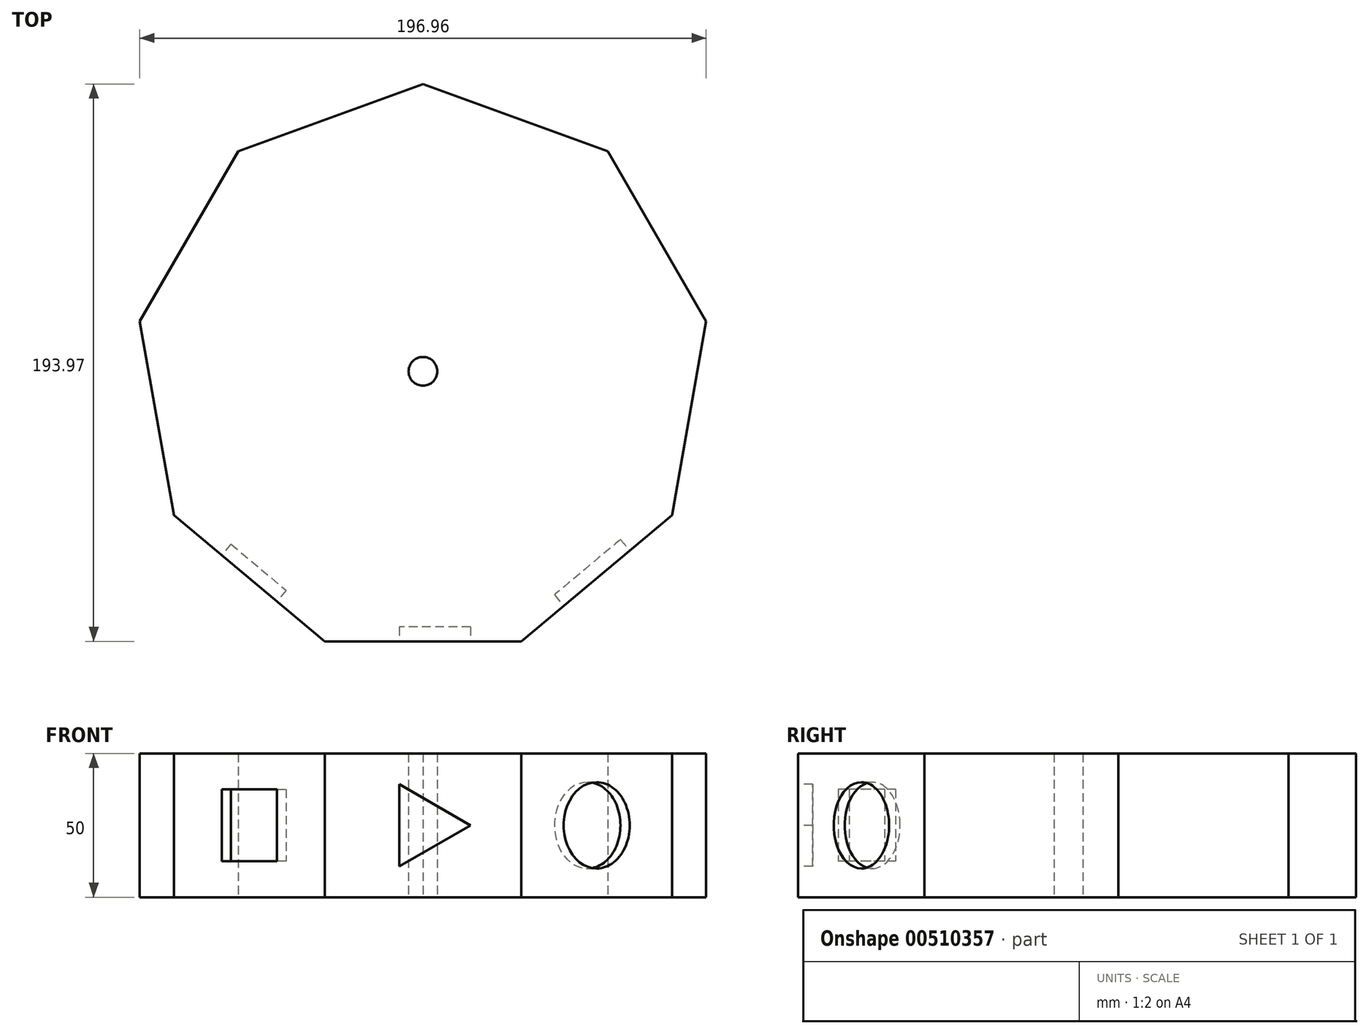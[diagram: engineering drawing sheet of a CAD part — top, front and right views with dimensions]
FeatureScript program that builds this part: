
annotation { "Feature Type Name" : "Feature", "Feature Type Description" : "" }
export const myFeature = defineFeature(function(context is Context, id is Id, definition is map)
    precondition{}
    {
        {
            var Q0;
            Q0=qCreatedBy(makeId("Top.planeOp"),FACE);
            var sketch = newSketch(context, id + "F0", { "sketchPlane" : qUnion([Q0])});
            skCircle(sketch, "E0.cCircle", {"center": v(0, 0) * mm, "radius": 100 * mm, "construction": true});
            skLineSegment(sketch, "E0.0", {"start": v(0, 100) * mm, "end": v(64.28, 76.6) * mm});
            skLineSegment(sketch, "E0.1", {"start": v(64.28, 76.6) * mm, "end": v(98.48, 17.36) * mm});
            skLineSegment(sketch, "E0.2", {"start": v(98.48, 17.36) * mm, "end": v(86.6, -50) * mm});
            skLineSegment(sketch, "E0.3", {"start": v(86.6, -50) * mm, "end": v(34.2, -93.97) * mm});
            skLineSegment(sketch, "E0.4", {"start": v(34.2, -93.97) * mm, "end": v(-34.2, -93.97) * mm});
            skLineSegment(sketch, "E0.5", {"start": v(-34.2, -93.97) * mm, "end": v(-86.6, -50) * mm});
            skLineSegment(sketch, "E0.6", {"start": v(-86.6, -50) * mm, "end": v(-98.48, 17.36) * mm});
            skLineSegment(sketch, "E0.7", {"start": v(-98.48, 17.36) * mm, "end": v(-64.28, 76.6) * mm});
            skLineSegment(sketch, "E0.8", {"start": v(-64.28, 76.6) * mm, "end": v(0, 100) * mm});
            skCircle(sketch, "E1", {"center": v(0, 0) * mm, "radius": 5 * mm});
            skSolve(sketch);
        }
        {
            var Q0;
            Q0=makeQuery(id+"F0.imprint","IMPRINT",FACE,{"disambiguationData":[TD([[makeQuery(id+"F0.imprint","IMPRINT",EDGE,{"derivedFrom":sQuery(id+"F0.wireOp",EDGE,"E0.0")}),-1.0]])]});
            extrude(context, id + "F1", {"entities" : qUnion([Q0]), "depth" : 50 * mm});
        }
        {
            var Q0;
            Q0=makeQuery(id+"F1.opExtrude","SWEPT_FACE",FACE,{"disambiguationData":[OSD([sQuery(id+"F0.wireOp",EDGE,"E0.3")])]});
            var sketch = newSketch(context, id + "F2", { "sketchPlane" : qUnion([Q0])});
            skLineSegment(sketch, "E2", {"start": v(0, 0) * mm, "end": v(0, 50) * mm, "construction": true});
            skLineSegment(sketch, "E3", {"start": v(-34.2, 25) * mm, "end": v(34.2, 25) * mm, "construction": true});
            skPoint(sketch, "E4", {"position": v(0, 25) * mm});
            skCircle(sketch, "E5", {"center": v(0, 25) * mm, "radius": 15 * mm});
            skSolve(sketch);
        }
        {
            var Q0;
            Q0=makeQuery(id+"F2.imprint","IMPRINT",FACE,{"disambiguationData":[TD([[makeQuery(id+"F2.imprint","IMPRINT",EDGE,{"derivedFrom":sQuery(id+"F2.wireOp",EDGE,"E5")}),1.0]])]});
            extrude(context, id + "F3", {"entities" : qUnion([Q0]), "operationType" : NewBodyOperationType.REMOVE, "oppositeDirection" : true, "depth" : 5 * mm});
        }
        {
            var Q0;
            Q0=makeQuery(id+"F1.opExtrude","SWEPT_FACE",FACE,{"disambiguationData":[OSD([sQuery(id+"F0.wireOp",EDGE,"E0.5")])]});
            var sketch = newSketch(context, id + "F4", { "sketchPlane" : qUnion([Q0])});
            skLineSegment(sketch, "E6", {"start": v(-34.2, 25) * mm, "end": v(34.2, 25) * mm, "construction": true});
            skLineSegment(sketch, "E7", {"start": v(0, 50) * mm, "end": v(0, 0) * mm, "construction": true});
            skLineSegment(sketch, "E8.bottom", {"start": v(-12.5, 37.5) * mm, "end": v(12.5, 37.5) * mm});
            skLineSegment(sketch, "E8.top", {"start": v(-12.5, 12.5) * mm, "end": v(12.5, 12.5) * mm});
            skLineSegment(sketch, "E8.left", {"start": v(-12.5, 37.5) * mm, "end": v(-12.5, 12.5) * mm});
            skLineSegment(sketch, "E8.right", {"start": v(12.5, 37.5) * mm, "end": v(12.5, 12.5) * mm});
            skSolve(sketch);
        }
        {
            var Q0;
            Q0=makeQuery(id+"F4.imprint","IMPRINT",FACE,{"disambiguationData":[TD([[makeQuery(id+"F4.imprint","IMPRINT",EDGE,{"derivedFrom":sQuery(id+"F4.wireOp",EDGE,"E8.bottom")}),-1.0]])]});
            extrude(context, id + "F5", {"entities" : qUnion([Q0]), "operationType" : NewBodyOperationType.REMOVE, "oppositeDirection" : true, "depth" : 5 * mm});
        }
        {
            var Q0;
            Q0=makeQuery(id+"F1.opExtrude","SWEPT_FACE",FACE,{"disambiguationData":[OSD([sQuery(id+"F0.wireOp",EDGE,"E0.4")])]});
            var sketch = newSketch(context, id + "F6", { "sketchPlane" : qUnion([Q0])});
            skLineSegment(sketch, "E9", {"start": v(0, 50) * mm, "end": v(0, 0) * mm, "construction": true});
            skLineSegment(sketch, "E10", {"start": v(-34.2, 25) * mm, "end": v(34.2, 25) * mm, "construction": true});
            skCircle(sketch, "E11.cCircle", {"center": v(0, 25) * mm, "radius": 16.5 * mm, "construction": true});
            skLineSegment(sketch, "E11.0", {"start": v(16.5, 25) * mm, "end": v(-8.25, 10.71) * mm});
            skLineSegment(sketch, "E11.1", {"start": v(-8.25, 10.71) * mm, "end": v(-8.25, 39.29) * mm});
            skLineSegment(sketch, "E11.2", {"start": v(-8.25, 39.29) * mm, "end": v(16.5, 25) * mm});
            skSolve(sketch);
        }
        {
            var Q0;
            Q0=makeQuery(id+"F6.imprint","IMPRINT",FACE,{"disambiguationData":[TD([[makeQuery(id+"F6.imprint","IMPRINT",EDGE,{"derivedFrom":sQuery(id+"F6.wireOp",EDGE,"E11.0")}),-1.0]])]});
            extrude(context, id + "F7", {"entities" : qUnion([Q0]), "operationType" : NewBodyOperationType.REMOVE, "oppositeDirection" : true, "depth" : 5 * mm});
        }
    });
